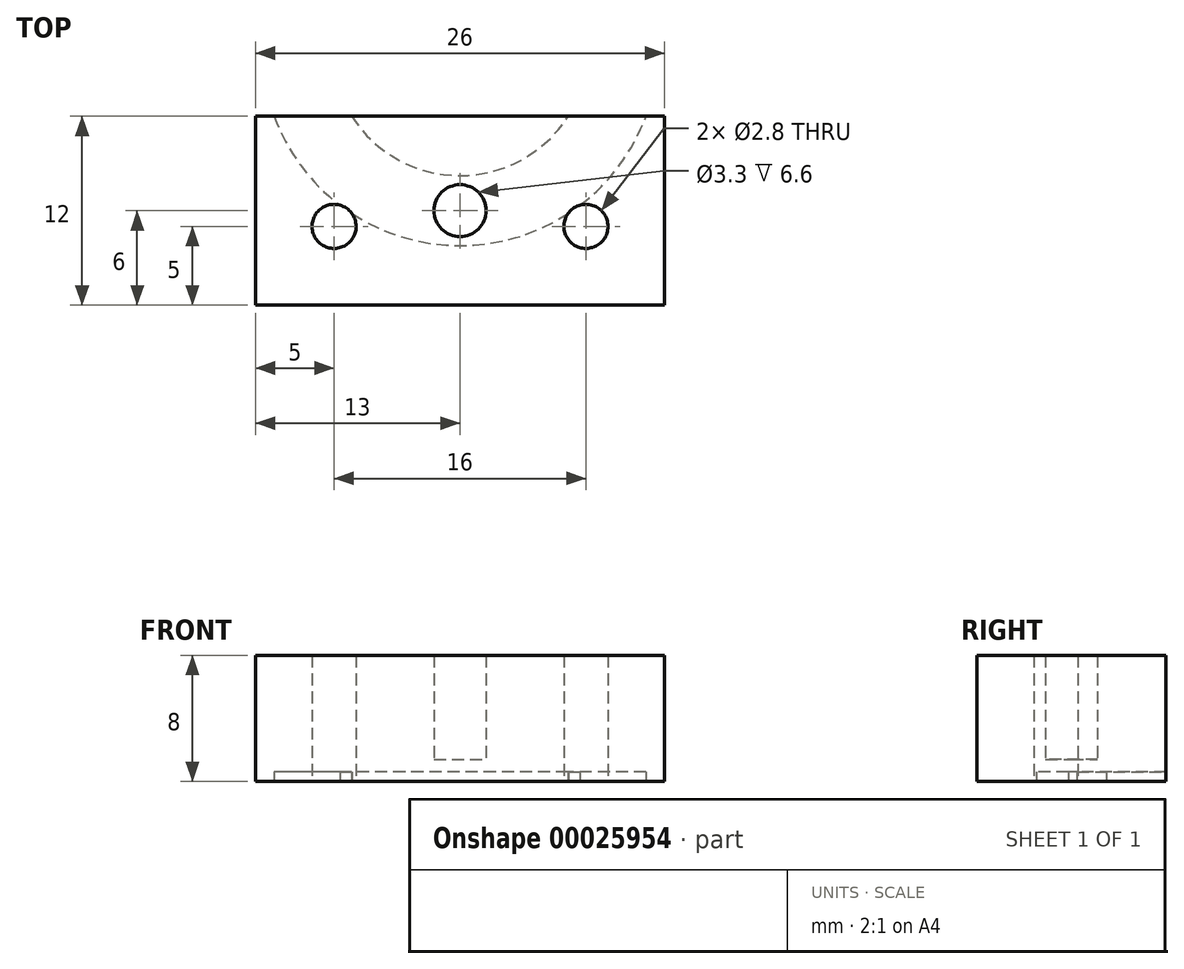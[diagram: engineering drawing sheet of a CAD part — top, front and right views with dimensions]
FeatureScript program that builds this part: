
annotation { "Feature Type Name" : "Feature", "Feature Type Description" : "" }
export const myFeature = defineFeature(function(context is Context, id is Id, definition is map)
    precondition{}
    {
        {
            var Q0;
            Q0=qCreatedBy(makeId("Top.planeOp"),FACE);
            var sketch = newSketch(context, id + "F0", { "sketchPlane" : qUnion([Q0])});
            skLineSegment(sketch, "E0.rect.bottom", {"start": v(13, -6) * mm, "end": v(-13, -6) * mm});
            skLineSegment(sketch, "E0.rect.top", {"start": v(13, 6) * mm, "end": v(-13, 6) * mm});
            skLineSegment(sketch, "E0.rect.left", {"start": v(13, -6) * mm, "end": v(13, 6) * mm});
            skLineSegment(sketch, "E0.rect.right", {"start": v(-13, -6) * mm, "end": v(-13, 6) * mm});
            skPoint(sketch, "E0.rect.middle", {"position": v(0, 0) * mm});
            skCircle(sketch, "E1", {"center": v(0, 0) * mm, "radius": 1.65 * mm});
            skCircle(sketch, "E2", {"center": v(-8, -1) * mm, "radius": 1.4 * mm});
            skLineSegment(sketch, "E3", {"start": v(0, 6) * mm, "end": v(0, -6) * mm, "construction": true});
            skCircle(sketch, "E4.MirrorC", {"center": v(8, -1) * mm, "radius": 1.4 * mm});
            skSolve(sketch);
        }
        {
            var Q0;
            Q0 = qSketchRegion(id + "F0", true);
            extrude(context, id + "F1", {"entities" : qUnion([Q0]), "depth" : 8 * mm});
        }
        {
            var Q0;
            Q0=makeQuery(id+"F1.opExtrude","CAP_FACE",FACE,{"disambiguationData":[OSD([sQuery(id+"F0.wireOp",EDGE,"E0.rect.bottom"),sQuery(id+"F0.wireOp",EDGE,"E0.rect.top"),sQuery(id+"F0.wireOp",EDGE,"E0.rect.left"),sQuery(id+"F0.wireOp",EDGE,"E0.rect.right"),sQuery(id+"F0.wireOp",EDGE,"E1"),sQuery(id+"F0.wireOp",EDGE,"E2"),sQuery(id+"F0.wireOp",EDGE,"E4.MirrorC")])],"isStart":true});
            var sketch = newSketch(context, id + "F2", { "sketchPlane" : qUnion([Q0])});
            skArc(sketch, "E5", {"start": v(6.88, -6) * mm, "mid": v(0, -2.22) * mm, "end": v(-6.88, -6) * mm});
            skArc(sketch, "E6", {"start": v(11.82, -6) * mm, "mid": v(0, 2.23) * mm, "end": v(-11.82, -6) * mm});
            skCircle(sketch, "E7", {"center": v(0, -10.38) * mm, "radius": 10.38 * mm, "construction": true});
            skLineSegment(sketch, "E8", {"start": v(-11.82, -6) * mm, "end": v(-6.88, -6) * mm});
            skLineSegment(sketch, "E9.trimOffspring", {"start": v(6.88, -6) * mm, "end": v(11.82, -6) * mm});
            skSolve(sketch);
        }
        {
            var Q0;
            Q0 = qSketchRegion(id + "F2", true);
            extrude(context, id + "F3", {"entities" : qUnion([Q0]), "operationType" : NewBodyOperationType.REMOVE, "oppositeDirection" : true, "depth" : .6 * mm});
        }
        {
            var Q0;
            Q0=makeQuery(id+"F3.boolean.opBoolean","COPY",FACE,{"derivedFrom":makeQuery(id+"F3.opExtrude","CAP_FACE",FACE,{"disambiguationData":[OSD([sQuery(id+"F2.wireOp",EDGE,"E5"),sQuery(id+"F2.wireOp",EDGE,"E6"),sQuery(id+"F2.wireOp",EDGE,"E8"),sQuery(id+"F2.wireOp",EDGE,"E9.trimOffspring")])],"isStart":false})});
            var sketch = newSketch(context, id + "F4", { "sketchPlane" : qUnion([Q0])});
            skLineSegment(sketch, "E10.rect.bottom", {"start": v(-2.52, 1.78) * mm, "end": v(2.52, 1.78) * mm});
            skLineSegment(sketch, "E10.rect.top", {"start": v(-2.52, -1.78) * mm, "end": v(2.52, -1.78) * mm});
            skLineSegment(sketch, "E10.rect.left", {"start": v(-2.52, 1.78) * mm, "end": v(-2.52, -1.78) * mm});
            skLineSegment(sketch, "E10.rect.right", {"start": v(2.52, 1.78) * mm, "end": v(2.52, -1.78) * mm});
            skPoint(sketch, "E10.rect.middle", {"position": v(0, 0) * mm});
            skSolve(sketch);
        }
        {
            var Q0;
            Q0 = qSketchRegion(id + "F4", true);
            extrude(context, id + "F5", {"entities" : qUnion([Q0]), "operationType" : NewBodyOperationType.ADD, "oppositeDirection" : true, "depth" : 0.8 * mm});
        }
    });
